# Revit family: OPTIMA_Compact_FF_DN20_5,0_RFA_2018
name_source: partatom
category: Pipe Accessories
revit_build: Autodesk Revit LT 2018 (Build: 20180329_1100(x64)
units: mm (PartAtom-declared; Revit-internal decimal feet)

## family parameters
Always vertical = Yes
Cut with Voids When Loaded = No
Part Type = Valve - Breaks Into
Round Connector Dimension = Use Diameter
Shared = No
Work Plane-Based = No

## types (6) — shared parameters
A = 30.00°
Description = Tlakově nezávislý 2-cestný regulační vyvažovací ventil (PICV)
H4 = 12 mm  [stored 0.0393701 ft]
H5 = 20 mm  [stored 0.0656168 ft]
L2D = 104 mm
L2D_Min = 3048 mm
Manufacturer = Hydronix
PLG0 = No
QmdConnectorList = 301;D;302;D
R5 = 5 mm  [stored 0.0164042 ft]
R6 = 12 mm  [stored 0.0393701 ft]
R7 = 17 mm  [stored 0.0557743 ft]
R8 = 14 mm  [stored 0.0459318 ft]
R9 = 8 mm  [stored 0.0262467 ft]
Type Comments = vnitřní závit; PN25; 0~120°C, bez měřicích vsuvek
URL = www.hydronix.cz
W2D = 32 mm  [stored 0.104987 ft]
magiPartTypeId = 304
magiProductFamilyId = 52eeb9fa0c9d42c987a78ea14b42d3

## per-type parameters (varying)
| type | CenSd_R1_6 | D | H1 | H2 | H3 | H6 | H6__ve | L1 | L1__ve | L2 | L3 | LL | MC Product Code | R1 | R2 | R3 | R4 | X | Z | magiProductId |
| OPTIMA Compact DN32 F-F 5.5mm | 23 mm | 32 mm | 46 mm  [stored 0.150919 ft] | 10 mm  [stored 0.0328084 ft] | 16 mm  [stored 0.0524934 ft] | 68 mm | -68 mm  [stored -0.223097 ft] | 19 mm  [stored 0.062336 ft] | -19 mm  [stored -0.062336 ft] | 67 mm | 13 mm  [stored 0.0426509 ft] | 52 mm  [stored 0.170604 ft] | 53-1354  (5/4" F-F; 5.5mm; Qmin-dpmin 550l/h-17.9kPa; Qmax-dpmin 4001l/h-28.0kPa; dpmax 800kPa) | 26 mm  [stored 0.0853018 ft] | 22 mm  [stored 0.0721785 ft] | 32 mm  [stored 0.104987 ft] | 29 mm  [stored 0.0951444 ft] | 13 mm  [stored 0.0426509 ft] | 1 mm  [stored 0.00328084 ft] | b339906595e54d959f7e36e14a5078 |
| OPTIMA Compact DN15 F-F 2.5mm | 13 mm  [stored 0.0426509 ft] | 15 mm | 26 mm  [stored 0.0853018 ft] | 8 mm  [stored 0.0262467 ft] | 18 mm  [stored 0.0590551 ft] | 57 mm  [stored 0.187008 ft] | -57 mm  [stored -0.187008 ft] | 14 mm  [stored 0.0459318 ft] | -14 mm | 48 mm  [stored 0.15748 ft] | 11 mm  [stored 0.0360892 ft] | 38 mm  [stored 0.124672 ft] | 53-1344  (1/2" F-F; 2.5mm; Qmin-dpmin 100l/h-14.9kPa; Qmax-dpmin 575l/h-18.5kPa; dpmax 800kPa) | 15 mm  [stored 0.0492126 ft] | 12 mm  [stored 0.0393701 ft] | 19 mm  [stored 0.062336 ft] | 19 mm  [stored 0.062336 ft] | 7 mm  [stored 0.0229659 ft] | 0 mm  [stored 0 ft] | 1f59e983221c4705b905dca277ac1b |
| OPTIMA Compact DN15 F-F 5.0mm | 13 mm  [stored 0.0426509 ft] | 15 mm | 26 mm  [stored 0.0853018 ft] | 8 mm  [stored 0.0262467 ft] | 18 mm  [stored 0.0590551 ft] | 57 mm  [stored 0.187008 ft] | -57 mm  [stored -0.187008 ft] | 14 mm  [stored 0.0459318 ft] | -14 mm | 48 mm  [stored 0.15748 ft] | 11 mm  [stored 0.0360892 ft] | 38 mm  [stored 0.124672 ft] | 53-1345  (1/2" F-F; 5.0mm; Qmin-dpmin 220l/h-16.0kPa; Qmax-dpmin 1330l/h-21.6Pa; dpmax 800kPa) | 15 mm  [stored 0.0492126 ft] | 12 mm  [stored 0.0393701 ft] | 19 mm  [stored 0.062336 ft] | 19 mm  [stored 0.062336 ft] | 7 mm  [stored 0.0229659 ft] | 0 mm  [stored 0 ft] | ed735bb751334d9b9367ccb2001bd8 |
| OPTIMA Compact DN20 F-F 5.0mm | 15 mm  [stored 0.0492126 ft] | 20 mm | 26 mm  [stored 0.0853018 ft] | 8 mm  [stored 0.0262467 ft] | 18 mm  [stored 0.0590551 ft] | 60 mm  [stored 0.19685 ft] | -60 mm | 14 mm  [stored 0.0459318 ft] | -14 mm | 51 mm | 11 mm  [stored 0.0360892 ft] | 40 mm | 53-1348  (3/4" F-F; 5.0mm; Qmin-dpmin 220l/h-16.0kPa; Qmax-dpmin 1330l/h-21.6Pa; dpmax 800kPa) | 18 mm  [stored 0.0590551 ft] | 14 mm  [stored 0.0459318 ft] | 19 mm  [stored 0.062336 ft] | 19 mm  [stored 0.062336 ft] | 10 mm  [stored 0.0328084 ft] | 0 mm  [stored 0 ft] | 3fe8f468b8a34e8b9375925b2f5228 |
| OPTIMA Compact DN20 F-F 5.5mm | 15 mm  [stored 0.0492126 ft] | 20 mm | 26 mm  [stored 0.0853018 ft] | 8 mm  [stored 0.0262467 ft] | 18 mm  [stored 0.0590551 ft] | 60 mm  [stored 0.19685 ft] | -60 mm | 14 mm  [stored 0.0459318 ft] | -14 mm | 51 mm | 11 mm  [stored 0.0360892 ft] | 40 mm | 53-1318  (3/4" F-F; 5.5mm; Qmin-dpmin 300l/h-17.8kPa; Qmax-dpmin 1800l/h-40.0Pa; dpmax 800kPa) | 18 mm  [stored 0.0590551 ft] | 14 mm  [stored 0.0459318 ft] | 19 mm  [stored 0.062336 ft] | 19 mm  [stored 0.062336 ft] | 10 mm  [stored 0.0328084 ft] | 0 mm  [stored 0 ft] | 3f04956b0a9346f48e327241883a91 |
| OPTIMA Compact DN25 F-F 5.5mm | 19 mm  [stored 0.062336 ft] | 25 mm | 43 mm  [stored 0.141076 ft] | 10 mm  [stored 0.0328084 ft] | 16 mm  [stored 0.0524934 ft] | 64 mm  [stored 0.209974 ft] | -64 mm  [stored -0.209974 ft] | 18 mm  [stored 0.0590551 ft] | -18 mm  [stored -0.0590551 ft] | 64 mm  [stored 0.209974 ft] | 13 mm  [stored 0.0426509 ft] | 50 mm  [stored 0.164042 ft] | 53-1353  (1" F-F; 5.5mm; Qmin-dpmin 600l/h-17.3kPa; Qmax-dpmin 3609l/h-23.0Pa; dpmax 800kPa) | 22 mm  [stored 0.0721785 ft] | 19 mm  [stored 0.062336 ft] | 32 mm  [stored 0.104987 ft] | 29 mm  [stored 0.0951444 ft] | 13 mm  [stored 0.0426509 ft] | 0 mm  [stored 0 ft] | a6a3417af38f4ebebee56b059e5e27 |

note: [stored X ft] marks values corroborated as IEEE doubles in the binary element streams (Revit-internal decimal feet)

## geometry (parser evidence)
native form markers: Sweep x1
no freeform markers — native parametric forms only
